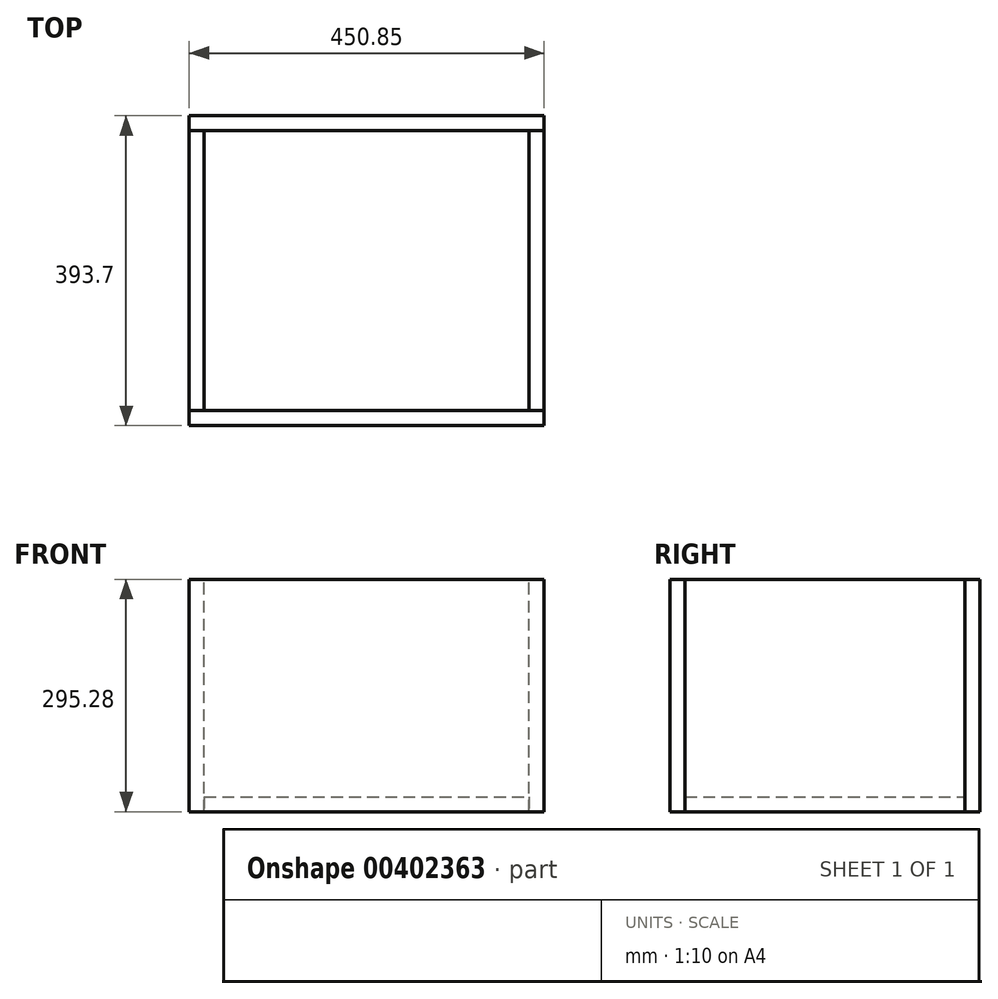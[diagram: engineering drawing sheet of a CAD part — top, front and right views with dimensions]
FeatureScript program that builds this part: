
annotation { "Feature Type Name" : "Feature", "Feature Type Description" : "" }
export const myFeature = defineFeature(function(context is Context, id is Id, definition is map)
    precondition{}
    {
        {
            var Q0;
            Q0=qCreatedBy(makeId("Front.planeOp"),FACE);
            var sketch = newSketch(context, id + "F0", { "sketchPlane" : qUnion([Q0])});
            skLineSegment(sketch, "E0.bottom", {"start": v(0, 0) * mm, "end": v(450.85, 0) * mm});
            skLineSegment(sketch, "E0.top", {"start": v(0, 295.28) * mm, "end": v(450.85, 295.28) * mm});
            skLineSegment(sketch, "E0.left", {"start": v(0, 0) * mm, "end": v(0, 295.28) * mm});
            skLineSegment(sketch, "E0.right", {"start": v(450.85, 0) * mm, "end": v(450.85, 295.28) * mm});
            skSolve(sketch);
        }
        {
            var Q0;
            Q0=makeQuery(id+"F0.imprint","IMPRINT",FACE,{"disambiguationData":[TD([[makeQuery(id+"F0.imprint","IMPRINT",EDGE,{"derivedFrom":sQuery(id+"F0.wireOp",EDGE,"E0.bottom")}),1.0]])]});
            extrude(context, id + "F1", {"entities" : qUnion([Q0]), "oppositeDirection" : true, "depth" : 19.05 * mm});
        }
        {
            var Q0;
            Q0=qCreatedBy(makeId("Right.planeOp"),FACE);
            var sketch = newSketch(context, id + "F2", { "sketchPlane" : qUnion([Q0])});
            skPoint(sketch, "E1.0", {"position": v(19.05, 0) * mm});
            skLineSegment(sketch, "E2.bottom", {"start": v(19.05, 0) * mm, "end": v(374.65, 0) * mm});
            skLineSegment(sketch, "E2.top", {"start": v(19.05, 295.28) * mm, "end": v(374.65, 295.28) * mm});
            skLineSegment(sketch, "E2.left", {"start": v(19.05, 0) * mm, "end": v(19.05, 295.28) * mm});
            skLineSegment(sketch, "E2.right", {"start": v(374.65, 0) * mm, "end": v(374.65, 295.28) * mm});
            skSolve(sketch);
        }
        {
            var Q0;
            Q0=makeQuery(id+"F2.imprint","IMPRINT",FACE,{"disambiguationData":[TD([[makeQuery(id+"F2.imprint","IMPRINT",EDGE,{"derivedFrom":sQuery(id+"F2.wireOp",EDGE,"E2.bottom")}),1.0]])]});
            extrude(context, id + "F3", {"entities" : qUnion([Q0]), "depth" : 19.05 * mm});
        }
        {
            var Q0;
            Q0=qCreatedBy(makeId("Front.planeOp"),FACE);
            cPlane(context, id + "F4", {"entities" : qUnion([Q0]), "cplaneType" : CPlaneType.OFFSET, "offset" : 196.85 * mm, "oppositeDirection" : true, "width" : 152.4 * mm, "height" : 152.4 * mm});
        }
        {
            var Q0;
            Q0=makeQuery(id+"F1.opExtrude","SWEPT_BODY",BODY,{"disambiguationData":[OSD([sQuery(id+"F0.wireOp",EDGE,"E0.bottom"),sQuery(id+"F0.wireOp",EDGE,"E0.top"),sQuery(id+"F0.wireOp",EDGE,"E0.left"),sQuery(id+"F0.wireOp",EDGE,"E0.right")])]});
            var Q1;
            Q1=qCreatedBy(id+"F4.planeOp",FACE);
            mirror(context, id + "F5", {"entities" : qUnion([Q0]), "mirrorPlane" : qUnion([Q1])});
        }
        {
            var Q0;
            Q0=qCreatedBy(makeId("Right.planeOp"),FACE);
            cPlane(context, id + "F6", {"entities" : qUnion([Q0]), "cplaneType" : CPlaneType.OFFSET, "offset" : 225.42 * mm, "width" : 152.4 * mm, "height" : 152.4 * mm});
        }
        {
            var Q0;
            Q0=makeQuery(id+"F3.opExtrude","SWEPT_BODY",BODY,{"disambiguationData":[OSD([sQuery(id+"F2.wireOp",EDGE,"E2.bottom"),sQuery(id+"F2.wireOp",EDGE,"E2.top"),sQuery(id+"F2.wireOp",EDGE,"E2.left"),sQuery(id+"F2.wireOp",EDGE,"E2.right")])]});
            var Q1;
            Q1=qCreatedBy(id+"F6.planeOp",FACE);
            mirror(context, id + "F7", {"entities" : qUnion([Q0]), "mirrorPlane" : qUnion([Q1])});
        }
        {
            var Q0;
            Q0=qCreatedBy(makeId("Top.planeOp"),FACE);
            var sketch = newSketch(context, id + "F8", { "sketchPlane" : qUnion([Q0])});
            skPoint(sketch, "E3.orphan", {"position": v(0, 19.05) * mm});
            skPoint(sketch, "E4.orphan", {"position": v(450.85, 19.05) * mm});
            skPoint(sketch, "E5.orphan", {"position": v(450.85, 374.65) * mm});
            skPoint(sketch, "E6.orphan", {"position": v(0, 374.65) * mm});
            skPoint(sketch, "E7.0.start.orphan", {"position": v(19.05, 19.05) * mm});
            skPoint(sketch, "E8.0.start.orphan", {"position": v(431.8, 19.05) * mm});
            skPoint(sketch, "E9.0.end.orphan", {"position": v(431.8, 374.65) * mm});
            skPoint(sketch, "E9.0.start.orphan", {"position": v(19.05, 374.65) * mm});
            skLineSegment(sketch, "E10.bottom", {"start": v(19.05, 19.05) * mm, "end": v(431.8, 19.05) * mm});
            skLineSegment(sketch, "E10.top", {"start": v(19.05, 374.65) * mm, "end": v(431.8, 374.65) * mm});
            skLineSegment(sketch, "E10.left", {"start": v(19.05, 19.05) * mm, "end": v(19.05, 374.65) * mm});
            skLineSegment(sketch, "E10.right", {"start": v(431.8, 19.05) * mm, "end": v(431.8, 374.65) * mm});
            skSolve(sketch);
        }
        {
            var Q0;
            Q0=makeQuery(id+"F8.imprint","IMPRINT",FACE,{"disambiguationData":[TD([[makeQuery(id+"F8.imprint","IMPRINT",EDGE,{"derivedFrom":sQuery(id+"F8.wireOp",EDGE,"E10.bottom")}),1.0]])]});
            extrude(context, id + "F9", {"entities" : qUnion([Q0]), "depth" : 19.05 * mm});
        }
    });
